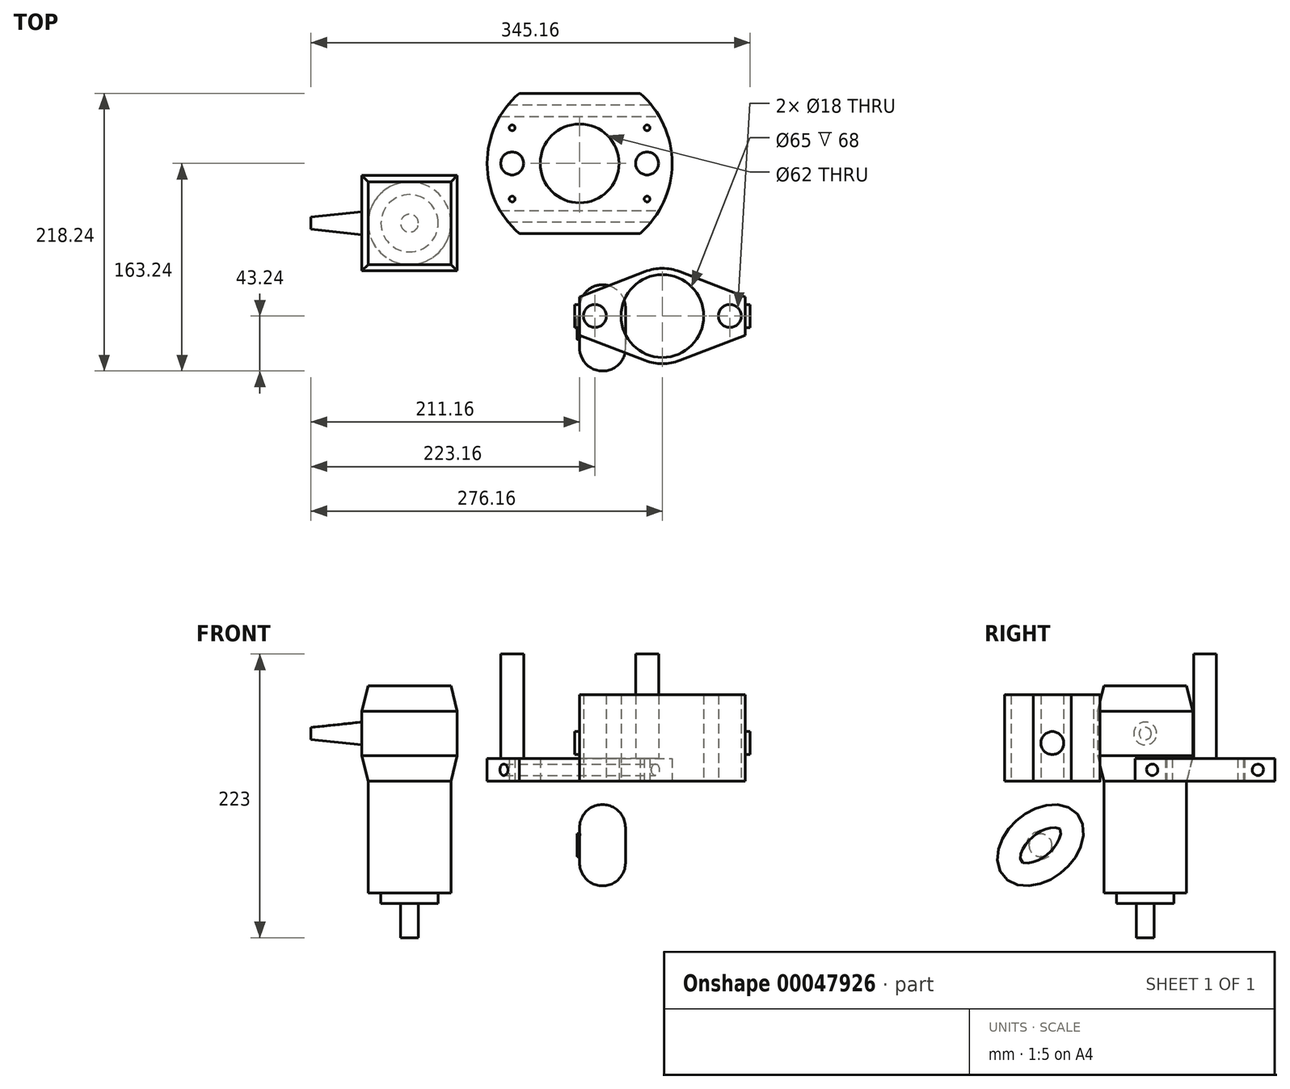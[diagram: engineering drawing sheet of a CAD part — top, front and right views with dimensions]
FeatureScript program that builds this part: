
annotation { "Feature Type Name" : "Feature", "Feature Type Description" : "" }
export const myFeature = defineFeature(function(context is Context, id is Id, definition is map)
    precondition{}
    {
        {
            var Q0;
            Q0=qCreatedBy(makeId("Top.planeOp"),FACE);
            var sketch = newSketch(context, id + "F0", { "sketchPlane" : qUnion([Q0])});
            skLineSegment(sketch, "E0", {"start": v(-47.5, 55) * mm, "end": v(47.5, 55) * mm});
            skLineSegment(sketch, "E1", {"start": v(47.5, -55) * mm, "end": v(-47.5, -55) * mm});
            skPoint(sketch, "E2", {"position": v(0, 55) * mm});
            skArc(sketch, "E3", {"start": v(47.5, 55) * mm, "mid": v(72.67, 0) * mm, "end": v(47.5, -55) * mm});
            skArc(sketch, "E4", {"start": v(-47.5, 55) * mm, "mid": v(-72.67, 0) * mm, "end": v(-47.5, -55) * mm});
            skLineSegment(sketch, "E5", {"start": v(-53, 0) * mm, "end": v(53, 0) * mm, "construction": true});
            skCircle(sketch, "E6", {"center": v(-53, 0) * mm, "radius": 9 * mm});
            skCircle(sketch, "E7", {"center": v(53, 0) * mm, "radius": 9 * mm});
            skCircle(sketch, "E8", {"center": v(0, 0) * mm, "radius": 31 * mm});
            skLineSegment(sketch, "E9", {"start": v(-72.67, -55) * mm, "end": v(-72.67, 55) * mm, "construction": true});
            skLineSegment(sketch, "E10", {"start": v(72.67, -55) * mm, "end": v(72.67, 55) * mm, "construction": true});
            skSolve(sketch);
        }
        {
            var Q0;
            Q0=makeQuery(id+"F0.imprint","IMPRINT",FACE,{"disambiguationData":[TD([[makeQuery(id+"F0.imprint","IMPRINT",EDGE,{"derivedFrom":sQuery(id+"F0.wireOp",EDGE,"E0")}),-1.0]])]});
            extrude(context, id + "F1", {"entities" : qUnion([Q0]), "depth" : 18 * mm});
        }
        {
            var Q0;
            Q0=makeQuery(id+"F0.imprint","IMPRINT",FACE,{"disambiguationData":[TD([[makeQuery(id+"F0.imprint","IMPRINT",EDGE,{"derivedFrom":sQuery(id+"F0.wireOp",EDGE,"E6")}),1.0]])]});
            var Q1;
            Q1=makeQuery(id+"F0.imprint","IMPRINT",FACE,{"disambiguationData":[TD([[makeQuery(id+"F0.imprint","IMPRINT",EDGE,{"derivedFrom":sQuery(id+"F0.wireOp",EDGE,"E7")}),1.0]])]});
            extrude(context, id + "F2", {"entities" : qUnion([Q0, Q1]), "operationType" : NewBodyOperationType.ADD, "depth" : 100 * mm});
        }
        {
            var Q0;
            Q0=qCreatedBy(makeId("Right.planeOp"),FACE);
            var sketch = newSketch(context, id + "F3", { "sketchPlane" : qUnion([Q0])});
            skCircle(sketch, "E11", {"center": v(-41.5, 9) * mm, "radius": 4.5 * mm});
            skCircle(sketch, "E12", {"center": v(41.5, 9) * mm, "radius": 4.5 * mm});
            skLineSegment(sketch, "E13", {"start": v(-41.5, 9) * mm, "end": v(41.5, 9) * mm, "construction": true});
            skPoint(sketch, "E14", {"position": v(0, 9) * mm});
            skSolve(sketch);
        }
        {
            var Q0;
            Q0 = qSketchRegion(id + "F3", true);
            extrude(context, id + "F4", {"entities" : qUnion([Q0]), "operationType" : NewBodyOperationType.REMOVE, "oppositeDirection" : true, "depth" : 200 * mm, "symmetric" : true});
        }
        {
            var Q0;
            Q0=qCreatedBy(makeId("Top.planeOp"),FACE);
            var sketch = newSketch(context, id + "F5", { "sketchPlane" : qUnion([Q0])});
            skLineSegment(sketch, "E15", {"start": v(0, -135) * mm, "end": v(0, -105) * mm});
            skLineSegment(sketch, "E16", {"start": v(0, -105) * mm, "end": v(51.43, -85.04) * mm});
            skArc(sketch, "E17", {"start": v(51.43, -85.04) * mm, "mid": v(65, -82.5) * mm, "end": v(78.57, -85.04) * mm});
            skLineSegment(sketch, "E18", {"start": v(78.57, -85.04) * mm, "end": v(130, -105) * mm});
            skLineSegment(sketch, "E19", {"start": v(130, -105) * mm, "end": v(130, -135) * mm});
            skLineSegment(sketch, "E20", {"start": v(130, -135) * mm, "end": v(78.57, -154.96) * mm});
            skArc(sketch, "E21", {"start": v(78.57, -154.96) * mm, "mid": v(65, -157.5) * mm, "end": v(51.43, -154.96) * mm});
            skLineSegment(sketch, "E22", {"start": v(0, -135) * mm, "end": v(51.43, -154.96) * mm});
            skPoint(sketch, "E23", {"position": v(0, -120) * mm});
            skPoint(sketch, "E24", {"position": v(130, -120) * mm});
            skLineSegment(sketch, "E25", {"start": v(0, -120) * mm, "end": v(130, -120) * mm, "construction": true});
            skCircle(sketch, "E26", {"center": v(65, -120) * mm, "radius": 32.5 * mm});
            skCircle(sketch, "E27", {"center": v(12, -120) * mm, "radius": 9 * mm});
            skCircle(sketch, "E28", {"center": v(118, -120) * mm, "radius": 9 * mm});
            skSolve(sketch);
        }
        {
            var Q0;
            Q0=makeQuery(id+"F5.imprint","IMPRINT",FACE,{"disambiguationData":[TD([[makeQuery(id+"F5.imprint","IMPRINT",EDGE,{"derivedFrom":sQuery(id+"F5.wireOp",EDGE,"E15")}),-1.0]])]});
            extrude(context, id + "F6", {"entities" : qUnion([Q0]), "depth" : 68 * mm});
        }
        {
            var Q0;
            Q0=makeQuery(id+"F6.opExtrude","SWEPT_FACE",FACE,{"disambiguationData":[OSD([sQuery(id+"F5.wireOp",EDGE,"E19")])]});
            var sketch = newSketch(context, id + "F7", { "sketchPlane" : qUnion([Q0])});
            skCircle(sketch, "E29", {"center": v(-120, 30) * mm, "radius": 9 * mm});
            skSolve(sketch);
        }
        {
            var Q0;
            Q0=makeQuery(id+"F7.imprint","IMPRINT",FACE,{"disambiguationData":[TD([[makeQuery(id+"F7.imprint","IMPRINT",EDGE,{"derivedFrom":sQuery(id+"F7.wireOp",EDGE,"E29")}),1.0]])]});
            extrude(context, id + "F8", {"entities" : qUnion([Q0]), "operationType" : NewBodyOperationType.ADD, "depth" : 4 * mm});
        }
        {
            var Q0;
            Q0=makeQuery(id+"F6.opExtrude","SWEPT_FACE",FACE,{"disambiguationData":[OSD([sQuery(id+"F5.wireOp",EDGE,"E15")])]});
            var sketch = newSketch(context, id + "F9", { "sketchPlane" : qUnion([Q0])});
            skCircle(sketch, "E30", {"center": v(120, 30) * mm, "radius": 9 * mm});
            skSolve(sketch);
        }
        {
            var Q0;
            Q0 = qSketchRegion(id + "F9", true);
            extrude(context, id + "F10", {"entities" : qUnion([Q0]), "operationType" : NewBodyOperationType.ADD, "depth" : 4 * mm});
        }
        {
            var Q0;
            Q0=qCreatedBy(makeId("Right.planeOp"),FACE);
            var sketch = newSketch(context, id + "F11", { "sketchPlane" : qUnion([Q0])});
            skEllipse(sketch, "E31", {"center": v(-129.31, -50.32) * mm, "majorRadius": 38 * mm, "minorRadius": 27 * mm, "majorAxis": v(0.77, 0.64)});
            skCircle(sketch, "E32", {"center": v(-129.31, -50.32) * mm, "radius": 9 * mm});
            skSolve(sketch);
        }
        {
            var Q0;
            Q0=makeQuery(id+"F11.imprint","IMPRINT",FACE,{"disambiguationData":[TD([[makeQuery(id+"F11.imprint","IMPRINT",EDGE,{"derivedFrom":sQuery(id+"F11.wireOp",EDGE,"E31")}),1.0]])]});
            var Q1;
            Q1=makeQuery(id+"F11.imprint","IMPRINT",FACE,{"disambiguationData":[TD([[makeQuery(id+"F11.imprint","IMPRINT",EDGE,{"derivedFrom":sQuery(id+"F11.wireOp",EDGE,"E32")}),1.0]])]});
            extrude(context, id + "F12", {"entities" : qUnion([Q0, Q1]), "depth" : 36 * mm});
        }
        {
            var Q0;
            Q0=makeQuery(id+"F12.opExtrude","CAP_EDGE",EDGE,{"disambiguationData":[OSD([sQuery(id+"F11.wireOp",EDGE,"E31")])],"isStart":false});
            var Q1;
            Q1=makeQuery(id+"F12.opExtrude","CAP_EDGE",EDGE,{"disambiguationData":[OSD([sQuery(id+"F11.wireOp",EDGE,"E31")])],"isStart":true});
            fillet(context, id + "F13", {"entities" : qUnion([Q0, Q1]), "radius" : 18 * mm, "allowEdgeOverflow" : false});
        }
        {
            var Q0;
            Q0=makeQuery(id+"F11.imprint","IMPRINT",FACE,{"disambiguationData":[TD([[makeQuery(id+"F11.imprint","IMPRINT",EDGE,{"derivedFrom":sQuery(id+"F11.wireOp",EDGE,"E32")}),1.0]])]});
            var Q1;
            Q1=sQuery(id+"F11.wireOp",EDGE,"E32");
            extrude(context, id + "F14", {"entities" : qUnion([Q0]), "operationType" : NewBodyOperationType.ADD, "surfaceEntities" : qUnion([Q1]), "depth" : 4 * mm, "symmetric" : true});
        }
        {
            var Q0;
            Q0=makeQuery(id+"F14.boolean.opBoolean","INTERSECT",EDGE,{"disambiguationData":[OD(1.0)],"derivedFrom":[makeQuery(id+"F12.opExtrude","CAP_FACE",FACE,{"disambiguationData":[OSD([sQuery(id+"F11.wireOp",EDGE,"E31")])],"isStart":true}),makeQuery(id+"F14.opExtrude","SWEPT_FACE",FACE,{"disambiguationData":[OSD([sQuery(id+"F11.wireOp",EDGE,"E32")])]})]});
            fillet(context, id + "F15", {"entities" : qUnion([Q0]), "radius" : 2 * mm, "tangentPropagation" : true, "allowEdgeOverflow" : false});
        }
        {
            var Q0;
            Q0=qCreatedBy(makeId("Top.planeOp"),FACE);
            var sketch = newSketch(context, id + "F16", { "sketchPlane" : qUnion([Q0])});
            skLineSegment(sketch, "E33.bottom", {"start": v(-171.16, -9.5) * mm, "end": v(-96.16, -9.5) * mm});
            skLineSegment(sketch, "E33.top", {"start": v(-171.16, -84.5) * mm, "end": v(-96.16, -84.5) * mm});
            skLineSegment(sketch, "E33.left", {"start": v(-171.16, -9.5) * mm, "end": v(-171.16, -84.5) * mm});
            skLineSegment(sketch, "E33.right", {"start": v(-96.16, -9.5) * mm, "end": v(-96.16, -84.5) * mm});
            skSolve(sketch);
        }
        {
            var Q0;
            Q0 = qSketchRegion(id + "F16", true);
            extrude(context, id + "F17", {"entities" : qUnion([Q0]), "depth" : 75 * mm});
        }
        {
            var Q0;
            Q0=makeQuery(id+"F17.opExtrude","CAP_EDGE",EDGE,{"disambiguationData":[OSD([sQuery(id+"F16.wireOp",EDGE,"E33.right")])],"isStart":false});
            chamfer(context, id + "F18", {"entities" : qUnion([Q0]), "chamferType" : ChamferType.TWO_OFFSETS, "width1" : 20 * mm, "oppositeDirection" : false, "width2" : 5 * mm, "tangentPropagation" : true});
        }
        {
            var Q0;
            Q0=makeQuery(id+"F17.opExtrude","CAP_FACE",FACE,{"disambiguationData":[OSD([sQuery(id+"F16.wireOp",EDGE,"E33.bottom"),sQuery(id+"F16.wireOp",EDGE,"E33.top"),sQuery(id+"F16.wireOp",EDGE,"E33.left"),sQuery(id+"F16.wireOp",EDGE,"E33.right")])],"isStart":true});
            var Q1;
            Q1=makeQuery(id+"F17.opExtrude","CAP_EDGE",EDGE,{"disambiguationData":[OSD([sQuery(id+"F16.wireOp",EDGE,"E33.top")])],"isStart":false});
            var Q2;
            Q2=makeQuery(id+"F17.opExtrude","CAP_EDGE",EDGE,{"disambiguationData":[OSD([sQuery(id+"F16.wireOp",EDGE,"E33.left")])],"isStart":false});
            var Q3;
            Q3=makeQuery(id+"F17.opExtrude","CAP_EDGE",EDGE,{"disambiguationData":[OSD([sQuery(id+"F16.wireOp",EDGE,"E33.bottom")])],"isStart":false});
            chamfer(context, id + "F19", {"entities" : qUnion([Q0, Q1, Q2, Q3]), "chamferType" : ChamferType.TWO_OFFSETS, "width1" : 20 * mm, "oppositeDirection" : true, "width2" : 5 * mm, "tangentPropagation" : true});
        }
        {
            var Q0;
            Q0=makeQuery(id+"F17.opExtrude","SWEPT_FACE",FACE,{"disambiguationData":[OSD([sQuery(id+"F16.wireOp",EDGE,"E33.left")])]});
            var sketch = newSketch(context, id + "F20", { "sketchPlane" : qUnion([Q0])});
            skCircle(sketch, "E34", {"center": v(47, 37.5) * mm, "radius": 9 * mm});
            skLineSegment(sketch, "E35", {"start": v(9.5, 55) * mm, "end": v(84.5, 20) * mm, "construction": true});
            skSolve(sketch);
        }
        {
            var Q0;
            Q0 = qSketchRegion(id + "F20", true);
            extrude(context, id + "F21", {"entities" : qUnion([Q0]), "operationType" : NewBodyOperationType.ADD, "depth" : 40 * mm, "hasDraft" : true, "draftAngle" : 6 * degree, "draftPullDirection" : true});
        }
        {
            var Q0;
            Q0=makeQuery(id+"F17.opExtrude","CAP_FACE",FACE,{"disambiguationData":[OSD([sQuery(id+"F16.wireOp",EDGE,"E33.bottom"),sQuery(id+"F16.wireOp",EDGE,"E33.top"),sQuery(id+"F16.wireOp",EDGE,"E33.left"),sQuery(id+"F16.wireOp",EDGE,"E33.right")])],"isStart":true});
            var sketch = newSketch(context, id + "F22", { "sketchPlane" : qUnion([Q0])});
            skLineSegment(sketch, "E36", {"start": v(-166.16, 79.5) * mm, "end": v(-101.16, 14.5) * mm, "construction": true});
            skCircle(sketch, "E37", {"center": v(-133.66, 47) * mm, "radius": 32.5 * mm});
            skSolve(sketch);
        }
        {
            var Q0;
            Q0 = qSketchRegion(id + "F22", true);
            extrude(context, id + "F23", {"entities" : qUnion([Q0]), "operationType" : NewBodyOperationType.ADD, "depth" : 88 * mm});
        }
        {
            var Q0;
            Q0=makeQuery(id+"F23.opExtrude","CAP_FACE",FACE,{"disambiguationData":[OSD([sQuery(id+"F22.wireOp",EDGE,"E37")])],"isStart":false});
            var sketch = newSketch(context, id + "F24", { "sketchPlane" : qUnion([Q0])});
            skCircle(sketch, "E38", {"center": v(-133.66, 47) * mm, "radius": 22.5 * mm});
            skSolve(sketch);
        }
        {
            var Q0;
            Q0 = qSketchRegion(id + "F24", true);
            extrude(context, id + "F25", {"entities" : qUnion([Q0]), "operationType" : NewBodyOperationType.ADD, "depth" : 8 * mm});
        }
        {
            var Q0;
            Q0=makeQuery(id+"F25.opExtrude","CAP_FACE",FACE,{"disambiguationData":[OSD([sQuery(id+"F24.wireOp",EDGE,"E38")])],"isStart":false});
            var sketch = newSketch(context, id + "F26", { "sketchPlane" : qUnion([Q0])});
            skCircle(sketch, "E39", {"center": v(-133.66, 47) * mm, "radius": 7 * mm});
            skSolve(sketch);
        }
        {
            var Q0;
            Q0 = qSketchRegion(id + "F26", true);
            extrude(context, id + "F27", {"entities" : qUnion([Q0]), "operationType" : NewBodyOperationType.ADD, "depth" : 27 * mm});
        }
        {
            var Q0;
            Q0=makeQuery(id+"F0.imprint","IMPRINT",FACE,{"disambiguationData":[TD([[makeQuery(id+"F0.imprint","IMPRINT",EDGE,{"derivedFrom":sQuery(id+"F0.wireOp",EDGE,"E0")}),-1.0]])]});
            var sketch = newSketch(context, id + "F28", { "sketchPlane" : qUnion([Q0])});
            skCircle(sketch, "E40", {"center": v(-53, 28) * mm, "radius": 2.25 * mm});
            skCircle(sketch, "E41", {"center": v(-53, -28) * mm, "radius": 2.25 * mm});
            skCircle(sketch, "E42", {"center": v(53, -28) * mm, "radius": 2.25 * mm});
            skCircle(sketch, "E43", {"center": v(53, 28) * mm, "radius": 2.25 * mm});
            skSolve(sketch);
        }
        {
            var Q0;
            Q0 = qSketchRegion(id + "F28", true);
            extrude(context, id + "F29", {"entities" : qUnion([Q0]), "operationType" : NewBodyOperationType.REMOVE, "depth" : 25 * mm});
        }
    });
